# Revit family: Basin-Semi-Recessed-Caroma Luna NTL1
name_source: partatom
category: Plumbing Fixtures
revit_build: Autodesk Revit 2015 (Build: 20160512_0715(x64)
units: mm (PartAtom-declared; Revit-internal decimal feet)

## types (1)
- Luna Semi Recessed - 0 Tap Holes
    1 Taphole = No
    3 Tapholes = No
    Assembly Code = D2010310
    CW Connection = No
    Cost = 0 $
    Default Elevation = 0 mm  [stored 0 ft]
    Depth_ANZRS = 153 mm  [stored 0.501969 ft]
    Description = Caroma Luna Semi Recessed Basin
    HW Connection = No
    Keynote = WB
    Length_ANZRS = 450 mm  [stored 1.47638 ft]
    Manufacturer = GWA Bathrooms & Kitchens
    Material_ANZRS = Porcelain-White-Caroma
    Model = 873505W
    ModifiedIssue_ANZRS = 20170216 $
    Spout Penetration = 100 mm  [stored 0.328084 ft]
    Tap Penetrations = 100 mm  [stored 0.328084 ft]
    Type Comments = Capacity: 4.8L to overflow, Overflow available only, Bracket included, White plug and chrome flush fitting waste included
    URL = https://specify.caroma.com.au
    Vent Connection = No
    WFU = 2
    Waste = Metal-Brass-Chrome
    Waste Connection = Yes
    Width_ANZRS = 380 mm

note: [stored X ft] marks values corroborated as IEEE doubles in the binary element streams (Revit-internal decimal feet)

## geometry (parser evidence)
native form markers: Blend x4, Sweep x2
no freeform markers — native parametric forms only
